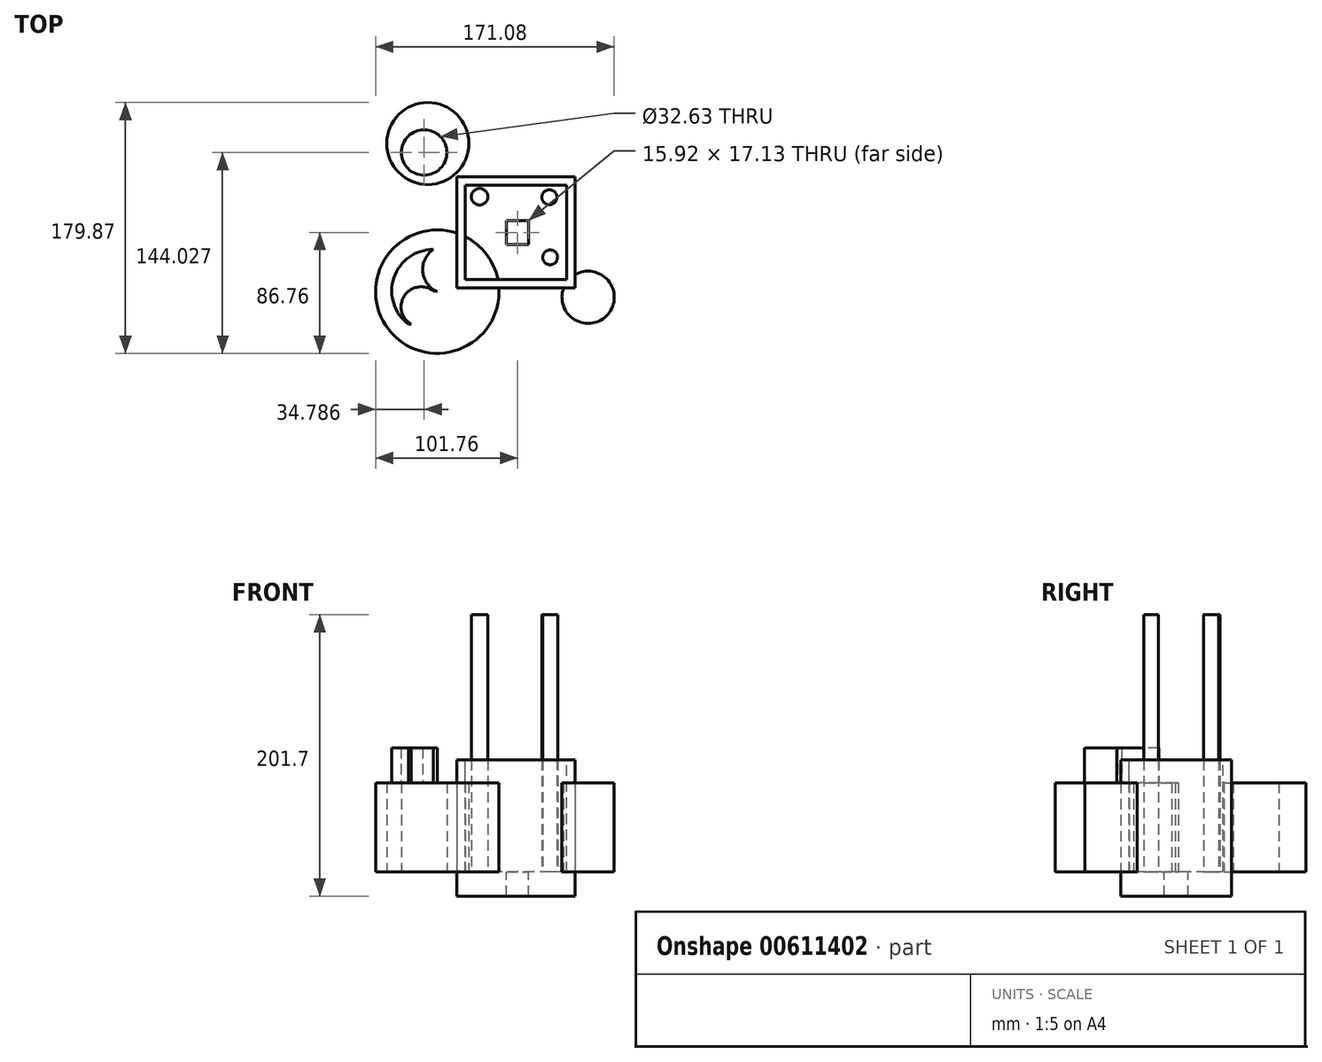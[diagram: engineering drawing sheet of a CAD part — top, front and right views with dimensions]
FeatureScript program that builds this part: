
annotation { "Feature Type Name" : "Feature", "Feature Type Description" : "" }
export const myFeature = defineFeature(function(context is Context, id is Id, definition is map)
    precondition{}
    {
        {
            var Q0;
            Q0=qCreatedBy(makeId("Top.planeOp"),FACE);
            var sketch = newSketch(context, id + "F0", { "sketchPlane" : qUnion([Q0])});
            skLineSegment(sketch, "E0.bottom", {"start": v(42.34, 39.79) * mm, "end": v(-42.34, 39.79) * mm});
            skLineSegment(sketch, "E0.top", {"start": v(42.34, -39.79) * mm, "end": v(-42.34, -39.79) * mm});
            skLineSegment(sketch, "E0.left", {"start": v(42.34, 39.79) * mm, "end": v(42.34, -39.79) * mm});
            skLineSegment(sketch, "E0.right", {"start": v(-42.34, 39.79) * mm, "end": v(-42.34, -39.79) * mm});
            skPoint(sketch, "E0.middle", {"position": v(0, 0) * mm});
            skSolve(sketch);
        }
        {
            var Q0;
            Q0=makeQuery(id+"F0.imprint","IMPRINT",FACE,{"disambiguationData":[TD([[makeQuery(id+"F0.imprint","IMPRINT",EDGE,{"derivedFrom":sQuery(id+"F0.wireOp",EDGE,"E0.bottom")}),1.0]])]});
            extrude(context, id + "F1", {"entities" : qUnion([Q0]), "depth" : 97.6 * mm, "offsetDistance" : 25 * mm});
        }
        {
            var Q0;
            Q0=makeQuery(id+"F1.opExtrude","CAP_FACE",FACE,{"disambiguationData":[OSD([sQuery(id+"F0.wireOp",EDGE,"E0.bottom"),sQuery(id+"F0.wireOp",EDGE,"E0.top"),sQuery(id+"F0.wireOp",EDGE,"E0.left"),sQuery(id+"F0.wireOp",EDGE,"E0.right")])],"isStart":false});
            var sketch = newSketch(context, id + "F2", { "sketchPlane" : qUnion([Q0])});
            skLineSegment(sketch, "E1.bottom", {"start": v(36.32, 33.76) * mm, "end": v(-36.32, 33.76) * mm});
            skLineSegment(sketch, "E1.top", {"start": v(36.32, -33.76) * mm, "end": v(-36.32, -33.76) * mm});
            skLineSegment(sketch, "E1.left", {"start": v(36.32, 33.76) * mm, "end": v(36.32, -33.76) * mm});
            skLineSegment(sketch, "E1.right", {"start": v(-36.32, 33.76) * mm, "end": v(-36.32, -33.76) * mm});
            skPoint(sketch, "E1.middle", {"position": v(0, 0) * mm});
            skSolve(sketch);
        }
        {
            var Q0;
            Q0=makeQuery(id+"F2.imprint","IMPRINT",FACE,{"disambiguationData":[TD([[makeQuery(id+"F2.imprint","IMPRINT",EDGE,{"derivedFrom":sQuery(id+"F2.wireOp",EDGE,"E1.bottom")}),1.0]])]});
            extrude(context, id + "F3", {"entities" : qUnion([Q0]), "operationType" : NewBodyOperationType.REMOVE, "oppositeDirection" : true, "depth" : 80.4 * mm, "offsetDistance" : 25 * mm});
        }
        {
            var Q0;
            Q0=makeQuery(id+"F3.boolean.opBoolean","COPY",FACE,{"derivedFrom":makeQuery(id+"F3.opExtrude","CAP_FACE",FACE,{"disambiguationData":[OSD([sQuery(id+"F2.wireOp",EDGE,"E1.bottom"),sQuery(id+"F2.wireOp",EDGE,"E1.top"),sQuery(id+"F2.wireOp",EDGE,"E1.left"),sQuery(id+"F2.wireOp",EDGE,"E1.right")])],"isStart":false})});
            var sketch = newSketch(context, id + "F4", { "sketchPlane" : qUnion([Q0])});
            skLineSegment(sketch, "E2.bottom", {"start": v(-6.77, 8.56) * mm, "end": v(9.15, 8.56) * mm});
            skLineSegment(sketch, "E2.top", {"start": v(-6.77, -8.56) * mm, "end": v(9.15, -8.56) * mm});
            skLineSegment(sketch, "E2.left", {"start": v(-6.77, 8.56) * mm, "end": v(-6.77, -8.56) * mm});
            skLineSegment(sketch, "E2.right", {"start": v(9.15, 8.56) * mm, "end": v(9.15, -8.56) * mm});
            skPoint(sketch, "E2.middle", {"position": v(1.19, 0) * mm});
            skSolve(sketch);
        }
        {
            var Q0;
            Q0=makeQuery(id+"F4.imprint","IMPRINT",FACE,{"disambiguationData":[TD([[makeQuery(id+"F4.imprint","IMPRINT",EDGE,{"derivedFrom":sQuery(id+"F4.wireOp",EDGE,"E2.bottom")}),-1.0]])]});
            extrude(context, id + "F5", {"entities" : qUnion([Q0]), "operationType" : NewBodyOperationType.REMOVE, "oppositeDirection" : true, "depth" : 25 * mm, "offsetDistance" : 25 * mm});
        }
        {
            var Q0;
            Q0=makeQuery(id+"F3.boolean.opBoolean","COPY",FACE,{"derivedFrom":makeQuery(id+"F3.opExtrude","CAP_FACE",FACE,{"disambiguationData":[OSD([sQuery(id+"F2.wireOp",EDGE,"E1.bottom"),sQuery(id+"F2.wireOp",EDGE,"E1.top"),sQuery(id+"F2.wireOp",EDGE,"E1.left"),sQuery(id+"F2.wireOp",EDGE,"E1.right")])],"isStart":false})});
            var sketch = newSketch(context, id + "F6", { "sketchPlane" : qUnion([Q0])});
            skCircle(sketch, "E3", {"center": v(-63.15, 63.7) * mm, "radius": 29.42 * mm});
            skCircle(sketch, "E4", {"center": v(-65.78, 57.27) * mm, "radius": 16.32 * mm});
            skCircle(sketch, "E5", {"center": v(51.78, -46.57) * mm, "radius": 18.74 * mm});
            skCircle(sketch, "E6", {"center": v(-56.3, -42.5) * mm, "radius": 44.26 * mm});
            skSolve(sketch);
        }
        {
            var Q0;
            Q0 = qSketchRegion(id + "F6", true);
            extrude(context, id + "F7", {"entities" : qUnion([Q0]), "operationType" : NewBodyOperationType.ADD, "depth" : 64 * mm, "offsetDistance" : 25 * mm});
        }
        {
            var Q0;
            {var subQ0=sQuery(id+"F6.wireOp",EDGE,"E6");Q0=makeQuery(id+"F7.boolean.opBoolean","SPLIT",FACE,{"disambiguationData":[TD([makeQuery(id+"F1.opExtrude","SWEPT_FACE",FACE,{"disambiguationData":[OSD([sQuery(id+"F0.wireOp",EDGE,"E0.top")])]})])],"derivedFrom":makeQuery(id+"F7.opExtrude","CAP_FACE",FACE,{"disambiguationData":[OSD([subQ0])],"isStart":false})});}
            var sketch = newSketch(context, id + "F8", { "sketchPlane" : qUnion([Q0])});
            skArc(sketch, "E7", {"start": v(-59.13, -12.23) * mm, "mid": v(-87.45, -32.58) * mm, "end": v(-76.88, -65.81) * mm});
            skArc(sketch, "E8", {"start": v(-59.27, -41.92) * mm, "mid": v(-79.9, -45.44) * mm, "end": v(-75.11, -65.81) * mm});
            skArc(sketch, "E9", {"start": v(-59.27, -12.32) * mm, "mid": v(-66.72, -28.29) * mm, "end": v(-56.3, -42.5) * mm});
            skPoint(sketch, "E10.orphan", {"position": v(-61.57, -12.32) * mm});
            skLineSegment(sketch, "E11", {"start": v(-75.11, -65.81) * mm, "end": v(-76.88, -65.81) * mm});
            skLineSegment(sketch, "E12", {"start": v(-59.27, -41.92) * mm, "end": v(-56.3, -42.5) * mm});
            skLineSegment(sketch, "E13", {"start": v(-59.27, -12.32) * mm, "end": v(-59.13, -12.23) * mm});
            skSolve(sketch);
        }
        {
            var Q0;
            Q0=makeQuery(id+"F8.imprint","IMPRINT",FACE,{"disambiguationData":[TD([[makeQuery(id+"F8.imprint","IMPRINT",EDGE,{"derivedFrom":sQuery(id+"F8.wireOp",EDGE,"E7")}),1.0]])]});
            extrude(context, id + "F9", {"entities" : qUnion([Q0]), "operationType" : NewBodyOperationType.ADD, "depth" : 25 * mm, "offsetDistance" : 25 * mm});
        }
        {
            var Q0;
            Q0=makeQuery(id+"F3.boolean.opBoolean","COPY",FACE,{"derivedFrom":makeQuery(id+"F3.opExtrude","CAP_FACE",FACE,{"disambiguationData":[OSD([sQuery(id+"F2.wireOp",EDGE,"E1.bottom"),sQuery(id+"F2.wireOp",EDGE,"E1.top"),sQuery(id+"F2.wireOp",EDGE,"E1.left"),sQuery(id+"F2.wireOp",EDGE,"E1.right")])],"isStart":false})});
            var sketch = newSketch(context, id + "F10", { "sketchPlane" : qUnion([Q0])});
            skCircle(sketch, "E14", {"center": v(-25.95, 25.55) * mm, "radius": 5.9 * mm});
            skCircle(sketch, "E15", {"center": v(24.02, 25.2) * mm, "radius": 5.37 * mm});
            skCircle(sketch, "E16", {"center": v(24.58, -17.91) * mm, "radius": 5.31 * mm});
            skSolve(sketch);
        }
        {
            var Q0;
            Q0=makeQuery(id+"F10.imprint","IMPRINT",FACE,{"disambiguationData":[TD([[makeQuery(id+"F10.imprint","IMPRINT",EDGE,{"derivedFrom":sQuery(id+"F10.wireOp",EDGE,"E14")}),1.0]])]});
            var Q1;
            Q1=makeQuery(id+"F10.imprint","IMPRINT",FACE,{"disambiguationData":[TD([[makeQuery(id+"F10.imprint","IMPRINT",EDGE,{"derivedFrom":sQuery(id+"F10.wireOp",EDGE,"E15")}),1.0]])]});
            var Q2;
            Q2=makeQuery(id+"F10.imprint","IMPRINT",FACE,{"disambiguationData":[TD([[makeQuery(id+"F10.imprint","IMPRINT",EDGE,{"derivedFrom":sQuery(id+"F10.wireOp",EDGE,"E16")}),1.0]])]});
            extrude(context, id + "F11", {"entities" : qUnion([Q0, Q1, Q2]), "operationType" : NewBodyOperationType.ADD, "depth" : 184.5 * mm, "offsetDistance" : 25 * mm});
        }
    });
